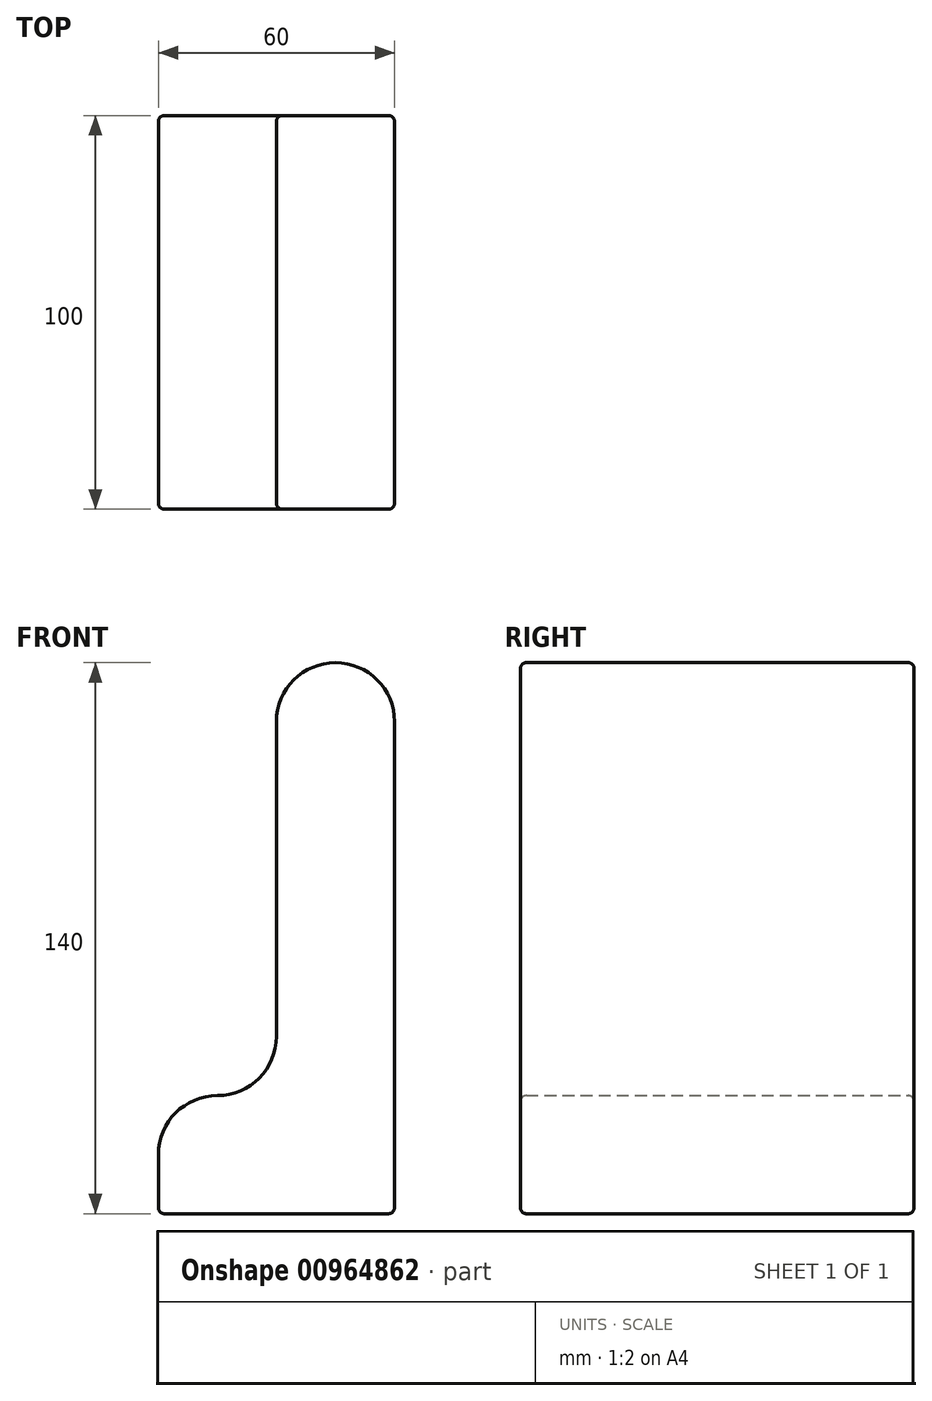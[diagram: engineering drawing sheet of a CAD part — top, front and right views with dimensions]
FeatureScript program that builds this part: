
annotation { "Feature Type Name" : "Feature", "Feature Type Description" : "" }
export const myFeature = defineFeature(function(context is Context, id is Id, definition is map)
    precondition{}
    {
        {
            var Q0;
            Q0=qCreatedBy(makeId("Front.planeOp"),FACE);
            var sketch = newSketch(context, id + "F0", { "sketchPlane" : qUnion([Q0])});
            skLineSegment(sketch, "E0.bottom", {"start": v(0, 0) * mm, "end": v(-60, 0) * mm});
            skLineSegment(sketch, "E0.top", {"start": v(0, 30) * mm, "end": v(-60, 30) * mm});
            skLineSegment(sketch, "E0.left", {"start": v(0, 0) * mm, "end": v(0, 30) * mm});
            skLineSegment(sketch, "E0.right", {"start": v(-60, 0) * mm, "end": v(-60, 30) * mm});
            skLineSegment(sketch, "E1.bottom", {"start": v(0, 30) * mm, "end": v(-30, 30) * mm});
            skLineSegment(sketch, "E1.top", {"start": v(0, 140) * mm, "end": v(-30, 140) * mm});
            skLineSegment(sketch, "E1.left", {"start": v(0, 30) * mm, "end": v(0, 140) * mm});
            skLineSegment(sketch, "E1.right", {"start": v(-30, 30) * mm, "end": v(-30, 140) * mm});
            skSolve(sketch);
        }
        {
            var Q0;
            Q0 = qSketchRegion(id + "F0", true);
            extrude(context, id + "F1", {"entities" : qUnion([Q0]), "depth" : 100 * mm, "offsetDistance" : 25 * mm});
        }
        {
            var Q0;
            Q0=makeQuery(id+"F1.opExtrude","SWEPT_EDGE",EDGE,{"disambiguationData":[OSD([sQuery(id+"F0.wireOp",EDGE,"E0.top"),sQuery(id+"F0.wireOp",EDGE,"E1.bottom"),sQuery(id+"F0.wireOp",EDGE,"E1.right")])]});
            var Q1;
            Q1=makeQuery(id+"F1.opExtrude","SWEPT_EDGE",EDGE,{"disambiguationData":[OSD([sQuery(id+"F0.wireOp",EDGE,"E0.top"),sQuery(id+"F0.wireOp",EDGE,"E0.right")])]});
            fillet(context, id + "F2", {"entities" : qUnion([Q0, Q1]), "radius" : 15 * mm, "tangentPropagation" : true, "allowEdgeOverflow" : false});
        }
        {
            var Q0;
            Q0=makeQuery(id+"F1.opExtrude","SWEPT_EDGE",EDGE,{"disambiguationData":[OSD([sQuery(id+"F0.wireOp",EDGE,"E1.top"),sQuery(id+"F0.wireOp",EDGE,"E1.right")])]});
            var Q1;
            Q1=makeQuery(id+"F1.opExtrude","SWEPT_EDGE",EDGE,{"disambiguationData":[OSD([sQuery(id+"F0.wireOp",EDGE,"E1.top"),sQuery(id+"F0.wireOp",EDGE,"E1.left")])]});
            fillet(context, id + "F3", {"entities" : qUnion([Q0, Q1]), "radius" : 15 * mm, "tangentPropagation" : true, "allowEdgeOverflow" : false});
        }
        {
            var Q0;
            Q0=makeQuery(id+"F1.opExtrude","SWEPT_EDGE",EDGE,{"disambiguationData":[OSD([sQuery(id+"F0.wireOp",EDGE,"E0.bottom"),sQuery(id+"F0.wireOp",EDGE,"E0.left")])]});
            var Q1;
            Q1=makeQuery(id+"F1.opExtrude","CAP_EDGE",EDGE,{"disambiguationData":[OSD([sQuery(id+"F0.wireOp",EDGE,"E0.bottom")])],"isStart":false});
            var Q2;
            Q2=makeQuery(id+"F1.opExtrude","SWEPT_EDGE",EDGE,{"disambiguationData":[OSD([sQuery(id+"F0.wireOp",EDGE,"E0.bottom"),sQuery(id+"F0.wireOp",EDGE,"E0.right")])]});
            var Q3;
            Q3=makeQuery(id+"F1.opExtrude","CAP_EDGE",EDGE,{"disambiguationData":[OSD([sQuery(id+"F0.wireOp",EDGE,"E0.bottom")])],"isStart":true});
            var Q4;
            Q4=makeQuery(id+"F1.opExtrude","CAP_EDGE",EDGE,{"disambiguationData":[OSD([sQuery(id+"F0.wireOp",EDGE,"E0.left"),sQuery(id+"F0.wireOp",EDGE,"E1.left")])],"isStart":false});
            var Q5;
            Q5=makeQuery(id+"F1.opExtrude","CAP_EDGE",EDGE,{"disambiguationData":[OSD([sQuery(id+"F0.wireOp",EDGE,"E0.left"),sQuery(id+"F0.wireOp",EDGE,"E1.left")])],"isStart":true});
            fillet(context, id + "F4", {"entities" : qUnion([Q0, Q1, Q2, Q3, Q4, Q5]), "radius" : 1.5 * mm, "tangentPropagation" : true, "allowEdgeOverflow" : false});
        }
    });
